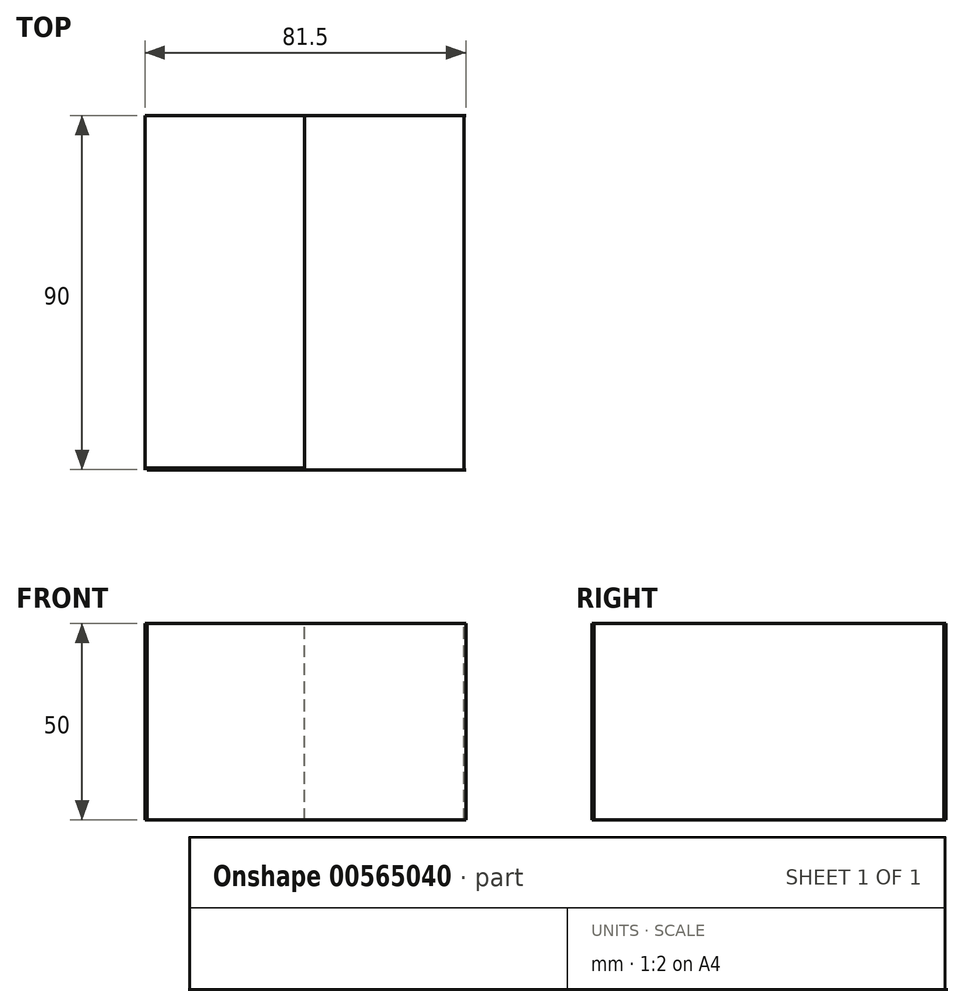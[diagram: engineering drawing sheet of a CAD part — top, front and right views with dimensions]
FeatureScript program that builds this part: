
annotation { "Feature Type Name" : "Feature", "Feature Type Description" : "" }
export const myFeature = defineFeature(function(context is Context, id is Id, definition is map)
    precondition{}
    {
        {
            var Q0;
            Q0=qCreatedBy(makeId("Top.planeOp"),FACE);
            var sketch = newSketch(context, id + "F0", { "sketchPlane" : qUnion([Q0])});
            skLineSegment(sketch, "E0.bottom", {"start": v(58.92, 3.3) * mm, "end": v(18.92, 3.3) * mm});
            skLineSegment(sketch, "E0.top", {"start": v(58.92, 92.3) * mm, "end": v(18.92, 92.3) * mm});
            skLineSegment(sketch, "E0.left", {"start": v(58.92, 3.3) * mm, "end": v(58.92, 92.3) * mm});
            skLineSegment(sketch, "E0.right", {"start": v(18.92, 3.3) * mm, "end": v(18.92, 92.3) * mm});
            skPoint(sketch, "E0.middle", {"position": v(38.92, 47.8) * mm});
            skLineSegment(sketch, "E1", {"start": v(18.92, 92.3) * mm, "end": v(18.42, 92.3) * mm});
            skLineSegment(sketch, "E2", {"start": v(18.92, 3.3) * mm, "end": v(18.42, 3.3) * mm});
            skLineSegment(sketch, "E3", {"start": v(18.42, 3.3) * mm, "end": v(18.42, 3.3) * mm});
            skLineSegment(sketch, "E4", {"start": v(18.42, 92.3) * mm, "end": v(18.42, 92.3) * mm});
            skLineSegment(sketch, "E5", {"start": v(18.42, 92.3) * mm, "end": v(18.42, 3.3) * mm});
            skLineSegment(sketch, "E6", {"start": v(18.42, 92.3) * mm, "end": v(-21.58, 92.3) * mm});
            skLineSegment(sketch, "E7", {"start": v(-21.58, 92.3) * mm, "end": v(-21.58, 92.3) * mm});
            skLineSegment(sketch, "E8", {"start": v(-21.58, 92.3) * mm, "end": v(-21.58, 3.3) * mm});
            skLineSegment(sketch, "E9", {"start": v(-21.58, 3.3) * mm, "end": v(18.42, 3.3) * mm});
            skLineSegment(sketch, "E10", {"start": v(-22.08, 92.8) * mm, "end": v(59.42, 92.8) * mm});
            skLineSegment(sketch, "E11", {"start": v(-21.58, 92.3) * mm, "end": v(-21.58, 92.8) * mm});
            skLineSegment(sketch, "E12", {"start": v(-21.58, 92.8) * mm, "end": v(-22.08, 92.8) * mm});
            skLineSegment(sketch, "E13", {"start": v(-22.08, 92.8) * mm, "end": v(-22.08, 2.8) * mm});
            skLineSegment(sketch, "E14", {"start": v(-21.58, 3.3) * mm, "end": v(-21.58, 2.8) * mm});
            skLineSegment(sketch, "E15", {"start": v(-21.58, 2.8) * mm, "end": v(-22.08, 2.8) * mm});
            skLineSegment(sketch, "E16", {"start": v(-21.58, 2.8) * mm, "end": v(59.42, 2.8) * mm});
            skLineSegment(sketch, "E17", {"start": v(59.42, 92.8) * mm, "end": v(59.42, 2.8) * mm});
            skLineSegment(sketch, "E18", {"start": v(58.92, 3.3) * mm, "end": v(58.92, 2.8) * mm});
            skLineSegment(sketch, "E19", {"start": v(58.92, 92.8) * mm, "end": v(58.92, 92.3) * mm});
            skSolve(sketch);
        }
        {
            var Q0;
            Q0=sQuery(id+"F0.wireOp",EDGE,"E10");
            var Q1;
            Q1=sQuery(id+"F0.wireOp",EDGE,"E13");
            var Q2;
            Q2=sQuery(id+"F0.wireOp",EDGE,"E0.left");
            var Q3;
            Q3=sQuery(id+"F0.wireOp",EDGE,"E5");
            var Q4;
            Q4=sQuery(id+"F0.wireOp",EDGE,"E9");
            var Q5;
            Q5=sQuery(id+"F0.wireOp",EDGE,"E16");
            extrude(context, id + "F1", {"bodyType" : ToolBodyType.SURFACE, "surfaceEntities" : qUnion([Q0, Q1, Q2, Q3, Q4, Q5]), "depth" : 50 * mm, "offsetDistance" : 25 * mm});
        }
    });
